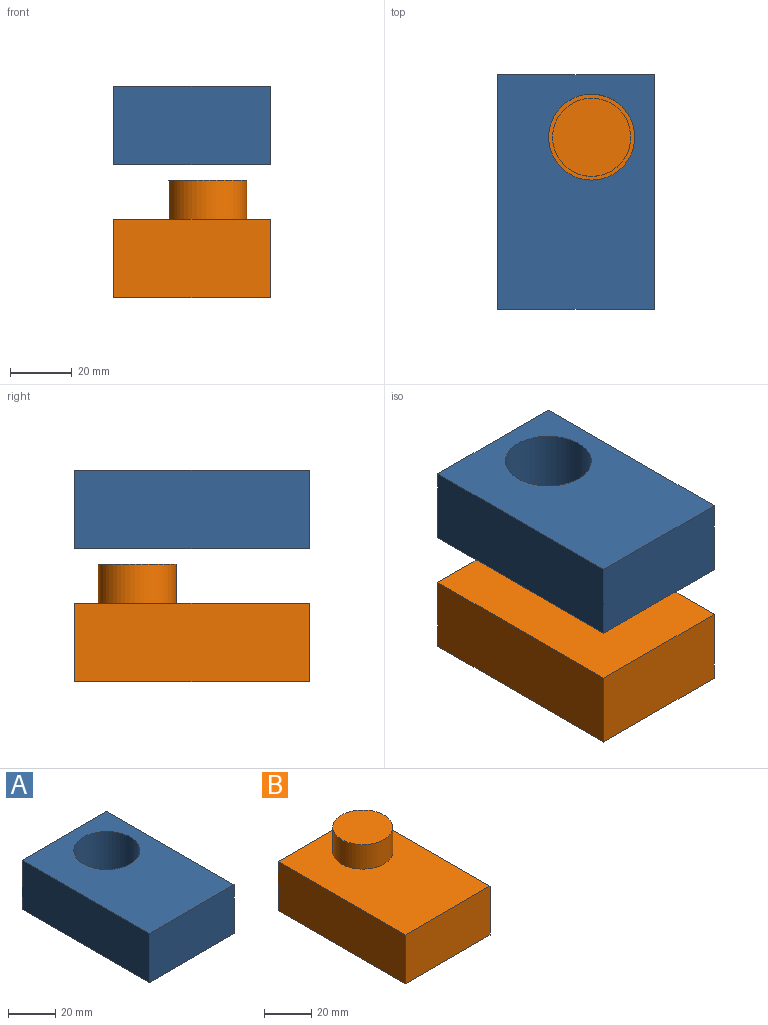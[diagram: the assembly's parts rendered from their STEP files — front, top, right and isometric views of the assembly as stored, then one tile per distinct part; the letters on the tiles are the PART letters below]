
ASSEMBLY  parts=2 mates=1
PART A: 7 faces, bbox 50.8x76.2x25.4 mm
  f0: plane 50.8x25.4mm, normal (0,1,0), area 1290.3mm2, adj f1,f4,f5,f6
  f1: plane 76.2x25.4mm, normal (-1,0,0), area 1935.5mm2, adj f0,f2,f5,f6
  f2: plane 50.8x25.4mm, normal (0,-1,0), area 1290.3mm2, adj f1,f4,f5,f6
  f3: cylinder r=13.97mm len=27.94mm, axis (0,0,1), area 2229.5mm2, adj f5,f6
  f4: plane 76.2x25.4mm, normal (1,0,0), area 1935.5mm2, adj f0,f2,f5,f6
  f5: plane 76.2x50.8mm, normal (0,0,-1), area 3257.8mm2, adj f0,f1,f2,f3,f4
  f6: plane 76.2x50.8mm, normal (0,0,1), area 3257.8mm2, adj f0,f1,f2,f3,f4
PART B: 8 faces, bbox 50.8x76.2x38.1 mm
  f0: plane 50.8x25.4mm, normal (0,-1,0), area 1290.3mm2, adj f1,f3,f4,f5
  f1: plane 76.2x25.4mm, normal (1,0,0), area 1935.5mm2, adj f0,f2,f4,f5
  f2: plane 50.8x25.4mm, normal (0,1,0), area 1290.3mm2, adj f1,f3,f4,f5
  f3: plane 76.2x25.4mm, normal (-1,0,0), area 1935.5mm2, adj f0,f2,f4,f5
  f4: plane 76.2x50.8mm, normal (0,0,1), area 3364.3mm2, adj f0,f1,f2,f3,f6
  f5: plane 76.2x50.8mm, normal (0,0,-1), area 3871mm2, adj f0,f1,f2,f3
  f6: cylinder r=12.7mm len=25.4mm, axis (0,0,-1), area 1013.4mm2, adj f4,f7
  f7: plane 25.4x25.4mm, normal (0,0,1), area 506.7mm2, adj f6
PLACE A t=(-121.22,-24.09,65.91)mm
PLACE B t=(-121.22,-24.09,-2.72)mm
MATE slider A.f3 <-> B.f6  axis (0,0,1) through (-116.14,-6.31,65.91)mm
